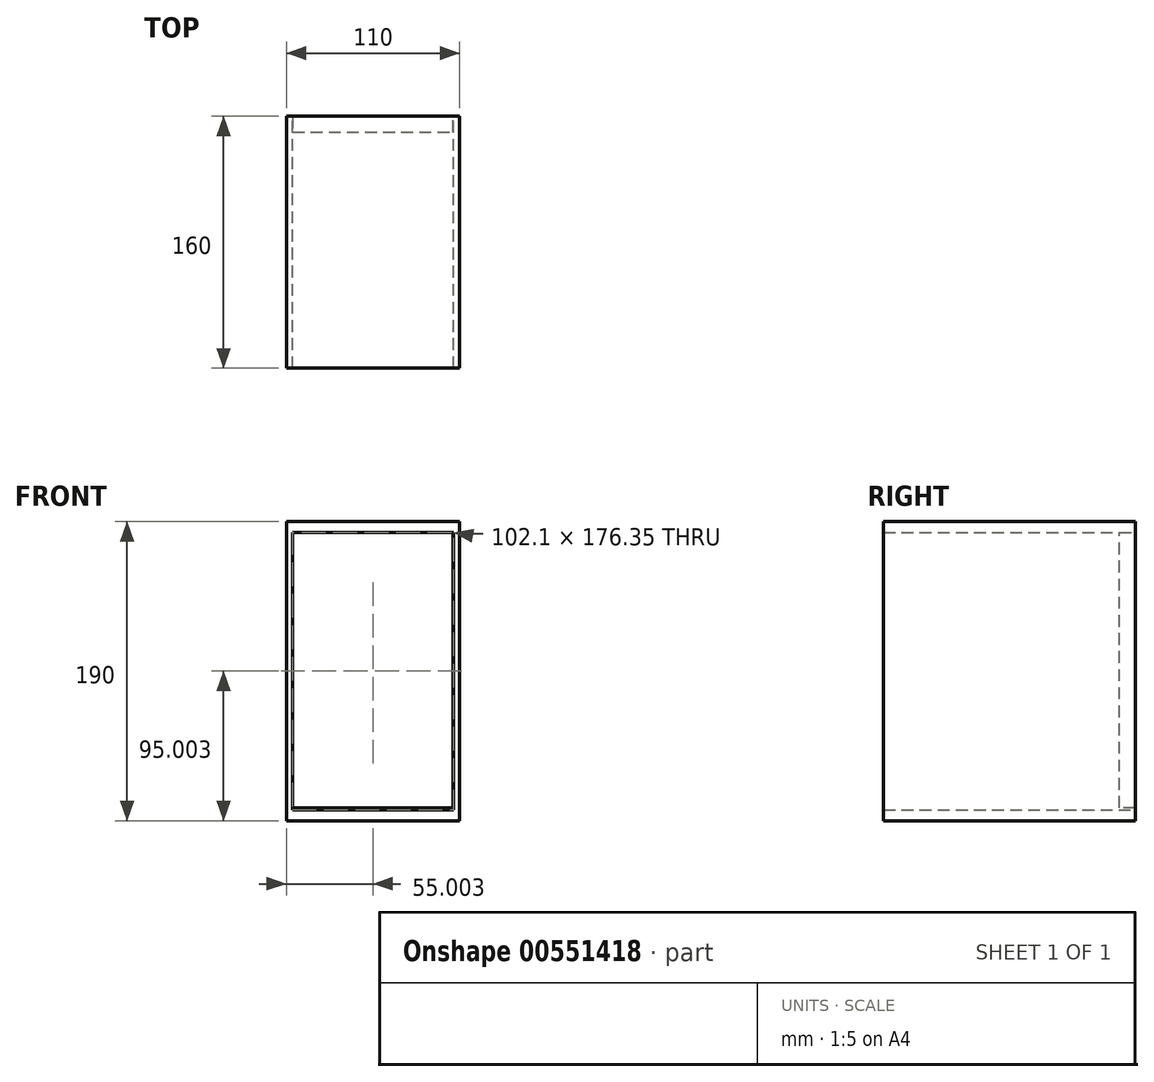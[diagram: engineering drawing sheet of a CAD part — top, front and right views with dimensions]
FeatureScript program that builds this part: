
annotation { "Feature Type Name" : "Feature", "Feature Type Description" : "" }
export const myFeature = defineFeature(function(context is Context, id is Id, definition is map)
    precondition{}
    {
        {
            var Q0;
            Q0=qCreatedBy(makeId("Front.planeOp"),FACE);
            var sketch = newSketch(context, id + "F0", { "sketchPlane" : qUnion([Q0])});
            skLineSegment(sketch, "E0", {"start": v(47.91, 91.18) * mm, "end": v(47.91, -98.82) * mm});
            skLineSegment(sketch, "E1", {"start": v(47.91, -98.82) * mm, "end": v(-62.09, -98.82) * mm});
            skLineSegment(sketch, "E2", {"start": v(-62.09, -98.82) * mm, "end": v(-62.09, 91.18) * mm});
            skLineSegment(sketch, "E3", {"start": v(-62.09, 91.18) * mm, "end": v(47.91, 91.18) * mm});
            skLineSegment(sketch, "E4", {"start": v(-58.14, 84.36) * mm, "end": v(43.96, 84.36) * mm});
            skLineSegment(sketch, "E5", {"start": v(43.96, 84.36) * mm, "end": v(43.96, -92) * mm});
            skLineSegment(sketch, "E6", {"start": v(43.96, -92) * mm, "end": v(-58.14, -92) * mm});
            skLineSegment(sketch, "E7", {"start": v(-58.14, -92) * mm, "end": v(-58.14, 84.36) * mm});
            skSolve(sketch);
        }
        {
            var Q0;
            Q0=makeQuery(id+"F0.imprint","IMPRINT",FACE,{"disambiguationData":[TD([[makeQuery(id+"F0.imprint","IMPRINT",EDGE,{"derivedFrom":sQuery(id+"F0.wireOp",EDGE,"E0")}),-1.0]])]});
            extrude(context, id + "F1", {"entities" : qUnion([Q0]), "depth" : 160 * mm, "offsetDistance" : 25.4 * mm});
        }
        {
            var Q0;
            Q0=qCreatedBy(makeId("Front.planeOp"),FACE);
            var sketch = newSketch(context, id + "F2", { "sketchPlane" : qUnion([Q0])});
            skLineSegment(sketch, "E8", {"start": v(43.78, 84.51) * mm, "end": v(43.78, -90.62) * mm});
            skLineSegment(sketch, "E9", {"start": v(43.78, -90.62) * mm, "end": v(-59.4, -90.62) * mm});
            skLineSegment(sketch, "E10", {"start": v(-59.4, -90.62) * mm, "end": v(-59.4, 84.51) * mm});
            skLineSegment(sketch, "E11", {"start": v(-59.4, 84.51) * mm, "end": v(43.78, 84.51) * mm});
            skSolve(sketch);
        }
        {
            var Q0;
            Q0=makeQuery(id+"F2.imprint","IMPRINT",FACE,{"disambiguationData":[TD([[makeQuery(id+"F2.imprint","IMPRINT",EDGE,{"derivedFrom":sQuery(id+"F2.wireOp",EDGE,"E8")}),-1.0]])]});
            extrude(context, id + "F3", {"entities" : qUnion([Q0]), "operationType" : NewBodyOperationType.ADD, "depth" : 10 * mm, "offsetDistance" : 25.4 * mm});
        }
    });
